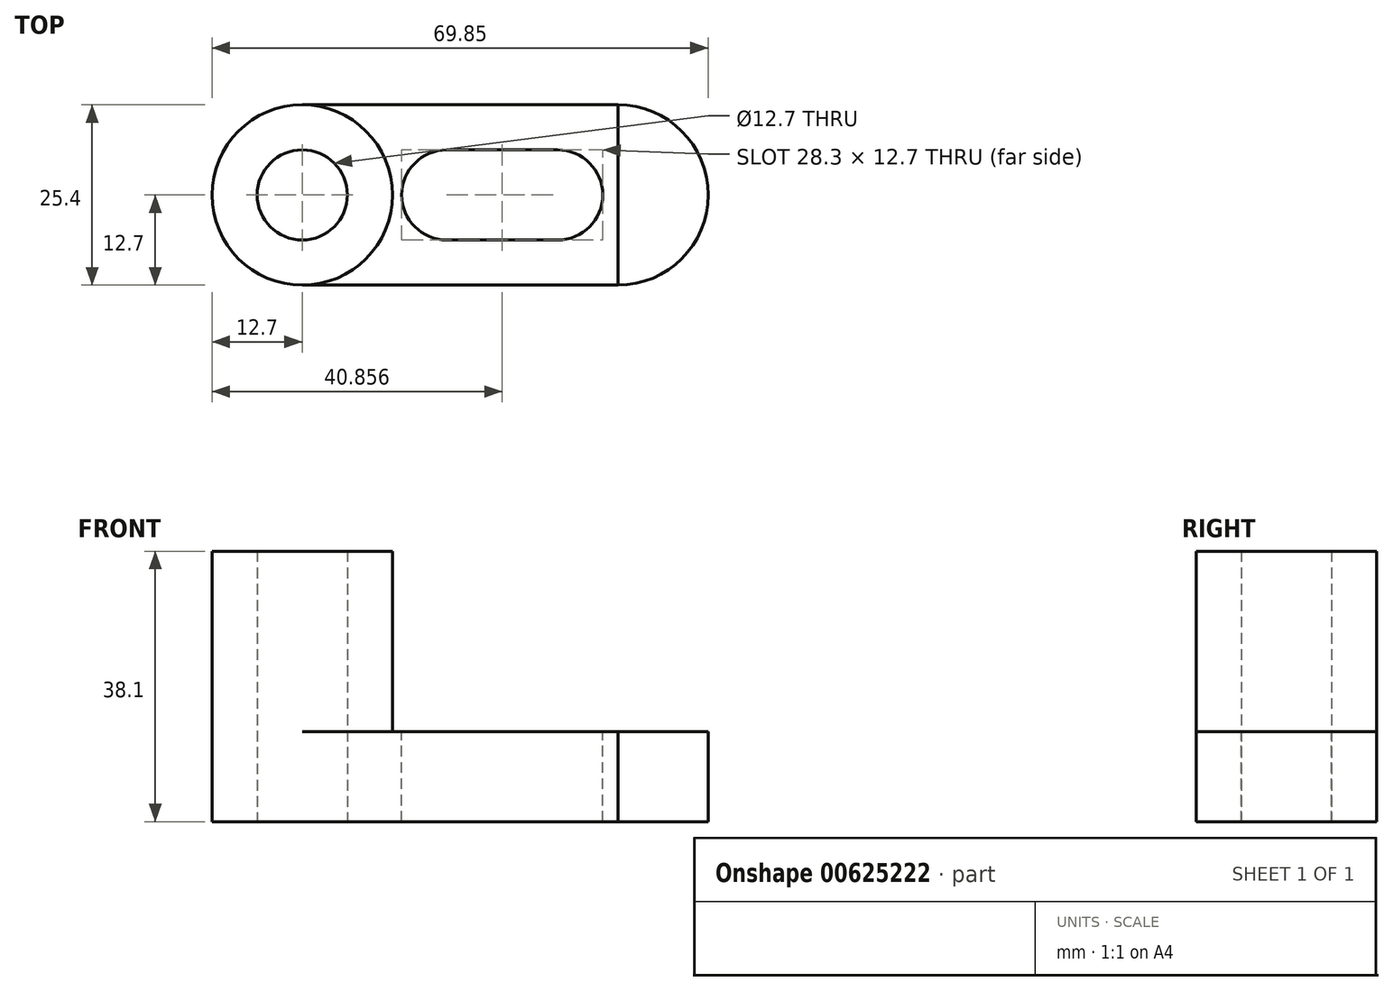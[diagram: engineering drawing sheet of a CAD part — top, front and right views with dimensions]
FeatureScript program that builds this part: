
annotation { "Feature Type Name" : "Feature", "Feature Type Description" : "" }
export const myFeature = defineFeature(function(context is Context, id is Id, definition is map)
    precondition{}
    {
        {
            var Q0;
            Q0=qCreatedBy(makeId("Front.planeOp"),FACE);
            var sketch = newSketch(context, id + "F0", { "sketchPlane" : qUnion([Q0])});
            skLineSegment(sketch, "E0", {"start": v(0, 0) * mm, "end": v(57.15, 0) * mm});
            skLineSegment(sketch, "E1", {"start": v(57.15, 0) * mm, "end": v(57.15, 12.7) * mm});
            skLineSegment(sketch, "E2", {"start": v(57.15, 12.7) * mm, "end": v(0, 12.7) * mm});
            skLineSegment(sketch, "E3", {"start": v(0, 12.7) * mm, "end": v(0, 0) * mm});
            skSolve(sketch);
        }
        {
            var Q0;
            Q0 = qSketchRegion(id + "F0", true);
            extrude(context, id + "F1", {"entities" : qUnion([Q0]), "depth" : 25.4 * mm, "offsetDistance" : 25.4 * mm});
        }
        {
            var Q0;
            Q0=makeQuery(id+"F1.opExtrude","SWEPT_FACE",FACE,{"disambiguationData":[OSD([sQuery(id+"F0.wireOp",EDGE,"E2")])]});
            var sketch = newSketch(context, id + "F2", { "sketchPlane" : qUnion([Q0])});
            skCircle(sketch, "E4", {"center": v(12.7, -12.7) * mm, "radius": 12.7 * mm});
            skPoint(sketch, "E4.centerSnap0", {"position": v(0, -12.7) * mm});
            skCircle(sketch, "E5", {"center": v(12.7, -12.7) * mm, "radius": 6.35 * mm});
            skSolve(sketch);
        }
        {
            var Q0;
            Q0 = qSketchRegion(id + "F2", true);
            extrude(context, id + "F3", {"entities" : qUnion([Q0]), "operationType" : NewBodyOperationType.ADD, "depth" : 25.4 * mm, "offsetDistance" : 25.4 * mm});
        }
        {
            var Q0;
            {var subQ0=sQuery(id+"F0.wireOp",EDGE,"E3");var subQ1=sQuery(id+"F0.wireOp",EDGE,"E2");var subQ2=makeQuery(id+"F1.opExtrude","SWEPT_FACE",FACE,{"disambiguationData":[OSD([subQ1])]});Q0=makeQuery(id+"F3.boolean.opBoolean","SPLIT",FACE,{"disambiguationData":[TD([makeQuery(id+"F1.opExtrude","CAP_FACE",FACE,{"disambiguationData":[OSD([sQuery(id+"F0.wireOp",EDGE,"E0"),sQuery(id+"F0.wireOp",EDGE,"E1"),subQ1,subQ0])],"isStart":false}),subQ2,makeQuery(id+"F1.opExtrude","SWEPT_FACE",FACE,{"disambiguationData":[OSD([subQ0])]}),makeQuery(id+"F3.opExtrude","SWEPT_FACE",FACE,{"disambiguationData":[OSD([sQuery(id+"F2.wireOp",EDGE,"E4")])]})])],"derivedFrom":subQ2});}
            var Q1;
            {var subQ0=sQuery(id+"F0.wireOp",EDGE,"E3");var subQ1=sQuery(id+"F0.wireOp",EDGE,"E2");var subQ2=makeQuery(id+"F1.opExtrude","SWEPT_FACE",FACE,{"disambiguationData":[OSD([subQ1])]});Q1=makeQuery(id+"F3.boolean.opBoolean","SPLIT",FACE,{"disambiguationData":[TD([makeQuery(id+"F1.opExtrude","CAP_FACE",FACE,{"disambiguationData":[OSD([sQuery(id+"F0.wireOp",EDGE,"E0"),sQuery(id+"F0.wireOp",EDGE,"E1"),subQ1,subQ0])],"isStart":true}),subQ2,makeQuery(id+"F1.opExtrude","SWEPT_FACE",FACE,{"disambiguationData":[OSD([subQ0])]}),makeQuery(id+"F3.opExtrude","SWEPT_FACE",FACE,{"disambiguationData":[OSD([sQuery(id+"F2.wireOp",EDGE,"E4")])]})])],"derivedFrom":subQ2});}
            extrude(context, id + "F4", {"entities" : qUnion([Q0, Q1]), "operationType" : NewBodyOperationType.REMOVE, "oppositeDirection" : true, "depth" : 25.4 * mm, "offsetDistance" : 25.4 * mm});
        }
        {
            var Q0;
            Q0=makeQuery(id+"F3.boolean.opBoolean","SPLIT",FACE,{"disambiguationData":[TD([makeQuery(id+"F3.opExtrude","SWEPT_FACE",FACE,{"disambiguationData":[OSD([sQuery(id+"F2.wireOp",EDGE,"E5")])]})])],"derivedFrom":makeQuery(id+"F1.opExtrude","SWEPT_FACE",FACE,{"disambiguationData":[OSD([sQuery(id+"F0.wireOp",EDGE,"E2")])]})});
            extrude(context, id + "F5", {"entities" : qUnion([Q0]), "operationType" : NewBodyOperationType.REMOVE, "oppositeDirection" : true, "depth" : 25.4 * mm, "offsetDistance" : 25.4 * mm});
        }
        {
            var Q0;
            {var subQ0=sQuery(id+"F0.wireOp",EDGE,"E2");var subQ1=makeQuery(id+"F1.opExtrude","SWEPT_FACE",FACE,{"disambiguationData":[OSD([subQ0])]});var subQ2=sQuery(id+"F0.wireOp",EDGE,"E1");var subQ3=sQuery(id+"F0.wireOp",EDGE,"E3");var subQ4=sQuery(id+"F0.wireOp",EDGE,"E0");Q0=makeQuery(id+"F3.boolean.opBoolean","SPLIT",FACE,{"disambiguationData":[TD([makeQuery(id+"F1.opExtrude","CAP_FACE",FACE,{"disambiguationData":[OSD([subQ4,subQ2,subQ0,subQ3])],"isStart":true}),makeQuery(id+"F1.opExtrude","CAP_FACE",FACE,{"disambiguationData":[OSD([subQ4,subQ2,subQ0,subQ3])],"isStart":false}),makeQuery(id+"F1.opExtrude","SWEPT_FACE",FACE,{"disambiguationData":[OSD([subQ2])]}),subQ1,makeQuery(id+"F3.opExtrude","SWEPT_FACE",FACE,{"disambiguationData":[OSD([sQuery(id+"F2.wireOp",EDGE,"E4")])]})])],"derivedFrom":subQ1});}
            var sketch = newSketch(context, id + "F6", { "sketchPlane" : qUnion([Q0])});
            skArc(sketch, "E6", {"start": v(57.15, -25.4) * mm, "mid": v(69.85, -12.7) * mm, "end": v(57.15, 0) * mm});
            skLineSegment(sketch, "E7", {"start": v(57.15, 0) * mm, "end": v(57.15, -25.4) * mm});
            skSolve(sketch);
        }
        {
            var Q0;
            Q0=makeQuery(id+"F6.imprint","IMPRINT",FACE,{"disambiguationData":[TD([[makeQuery(id+"F6.imprint","IMPRINT",EDGE,{"derivedFrom":sQuery(id+"F6.wireOp",EDGE,"E6")}),1.0]])]});
            extrude(context, id + "F7", {"entities" : qUnion([Q0]), "oppositeDirection" : true, "depth" : 12.7 * mm, "offsetDistance" : 25.4 * mm});
        }
        {
            var Q0;
            {var subQ0=sQuery(id+"F0.wireOp",EDGE,"E2");var subQ1=makeQuery(id+"F1.opExtrude","SWEPT_FACE",FACE,{"disambiguationData":[OSD([subQ0])]});var subQ2=sQuery(id+"F0.wireOp",EDGE,"E1");var subQ3=sQuery(id+"F0.wireOp",EDGE,"E3");var subQ4=sQuery(id+"F0.wireOp",EDGE,"E0");Q0=makeQuery(id+"F3.boolean.opBoolean","SPLIT",FACE,{"disambiguationData":[TD([makeQuery(id+"F1.opExtrude","CAP_FACE",FACE,{"disambiguationData":[OSD([subQ4,subQ2,subQ0,subQ3])],"isStart":true}),makeQuery(id+"F1.opExtrude","CAP_FACE",FACE,{"disambiguationData":[OSD([subQ4,subQ2,subQ0,subQ3])],"isStart":false}),makeQuery(id+"F1.opExtrude","SWEPT_FACE",FACE,{"disambiguationData":[OSD([subQ2])]}),subQ1,makeQuery(id+"F3.opExtrude","SWEPT_FACE",FACE,{"disambiguationData":[OSD([sQuery(id+"F2.wireOp",EDGE,"E4")])]})])],"derivedFrom":subQ1});}
            var sketch = newSketch(context, id + "F8", { "sketchPlane" : qUnion([Q0])});
            skCircle(sketch, "E8", {"center": v(33.05, -12.7) * mm, "radius": 6.35 * mm});
            skPoint(sketch, "E8.centerSnap0", {"position": v(25.4, -12.7) * mm});
            skCircle(sketch, "E9", {"center": v(48.66, -12.7) * mm, "radius": 6.35 * mm});
            skLineSegment(sketch, "E10", {"start": v(33.05, -6.35) * mm, "end": v(48.66, -6.35) * mm});
            skLineSegment(sketch, "E11", {"start": v(33.05, -19.05) * mm, "end": v(48.66, -19.05) * mm});
            skSolve(sketch);
        }
        {
            var Q0;
            Q0 = qSketchRegion(id + "F8", true);
            extrude(context, id + "F9", {"entities" : qUnion([Q0]), "operationType" : NewBodyOperationType.REMOVE, "oppositeDirection" : true, "depth" : 25.4 * mm, "offsetDistance" : 25.4 * mm});
        }
    });
